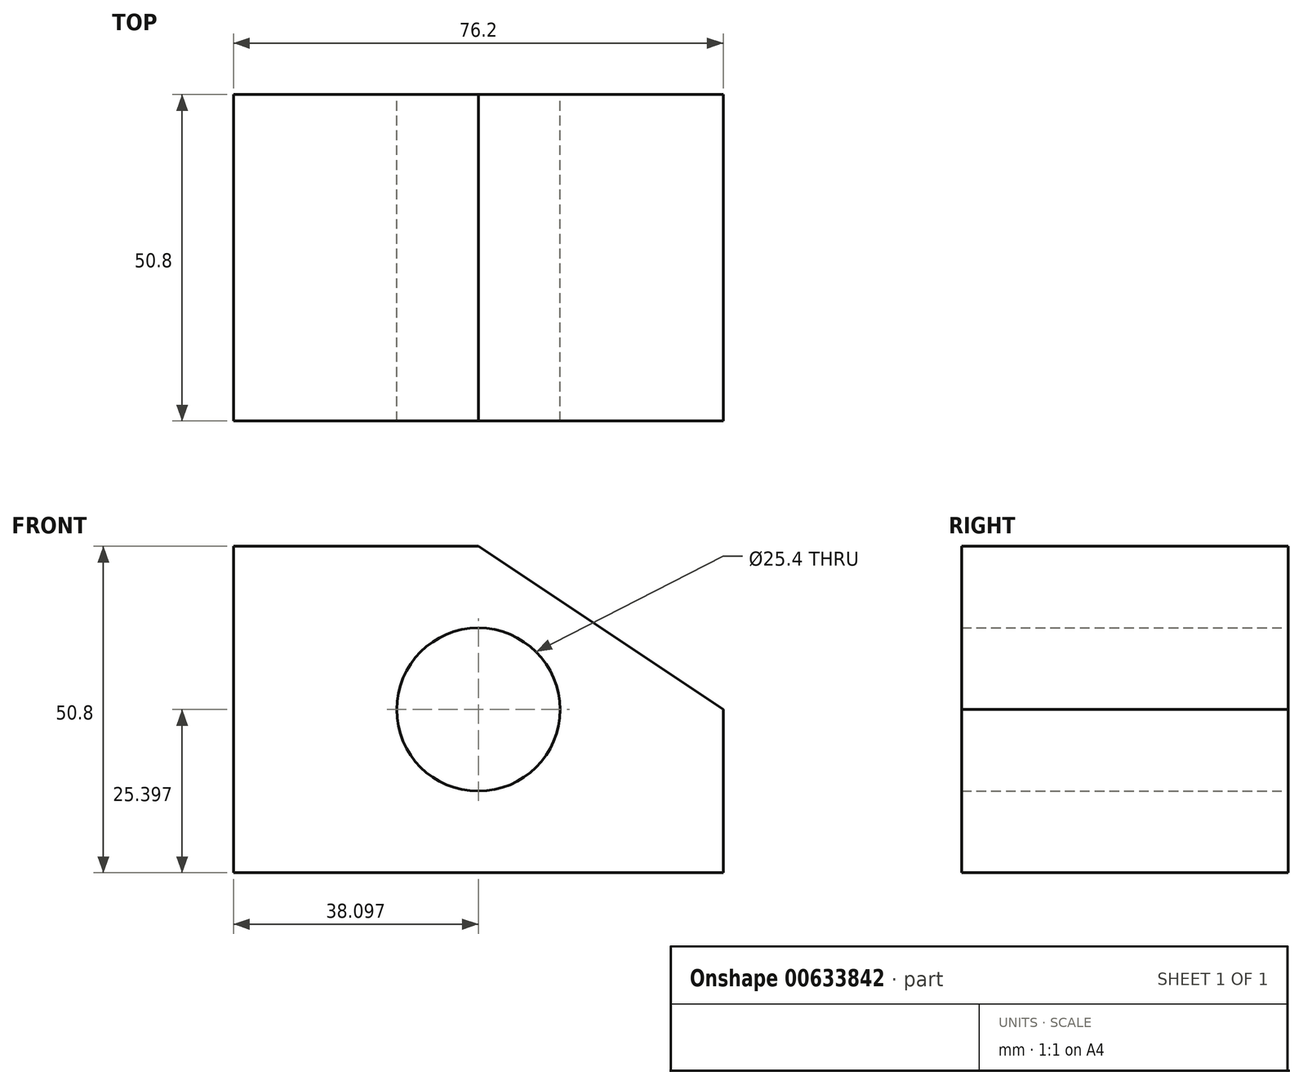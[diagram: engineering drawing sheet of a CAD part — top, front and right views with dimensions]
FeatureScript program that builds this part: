
annotation { "Feature Type Name" : "Feature", "Feature Type Description" : "" }
export const myFeature = defineFeature(function(context is Context, id is Id, definition is map)
    precondition{}
    {
        {
            var Q0;
            Q0=qCreatedBy(makeId("Front.planeOp"),FACE);
            var sketch = newSketch(context, id + "F0", { "sketchPlane" : qUnion([Q0])});
            skLineSegment(sketch, "E0", {"start": v(-57.12, 28.33) * mm, "end": v(-57.12, -22.47) * mm});
            skLineSegment(sketch, "E1", {"start": v(-57.12, 28.33) * mm, "end": v(-19.02, 28.33) * mm});
            skLineSegment(sketch, "E2", {"start": v(-19.02, 28.33) * mm, "end": v(19.08, 2.93) * mm});
            skLineSegment(sketch, "E3", {"start": v(19.08, 2.93) * mm, "end": v(19.08, -22.47) * mm});
            skLineSegment(sketch, "E4", {"start": v(-57.12, -22.47) * mm, "end": v(19.08, -22.47) * mm});
            skPoint(sketch, "E5", {"position": v(-19.02, 2.93) * mm});
            skCircle(sketch, "E6", {"center": v(-19.02, 2.93) * mm, "radius": 12.7 * mm});
            skSolve(sketch);
        }
        {
            var Q0;
            Q0=makeQuery(id+"F0.imprint","IMPRINT",FACE,{"disambiguationData":[TD([[makeQuery(id+"F0.imprint","IMPRINT",EDGE,{"derivedFrom":sQuery(id+"F0.wireOp",EDGE,"E0")}),1.0]])]});
            extrude(context, id + "F1", {"entities" : qUnion([Q0]), "depth" : 50.8 * mm, "offsetDistance" : 25.4 * mm});
        }
    });
